# Revit family: Ray L-78
name_source: partatom
category: Lighting Fixtures
revit_build: Autodesk Revit 2014 (Build: 20140709_2115(x64)
units: mm (PartAtom-declared; Revit-internal decimal feet)

## types (1)
- 78-1/4"L 20-1/4"W x 6"H
    Adjustable Suspension Height = 48"
    Cables = (2)3/64" stainless steel cables
    Canopy Type = Canopy
    Color Filter = 16777215
    Diffuser = White Opal Acrylic
    Dimming Compatibility = 0-10v
    Dimming Lamp Color Temperature Shift = <None>
    Driver = (2) 100W
    Emit from Line Length = 60"
    Hardware = Stainless Steel Cables
    Height = 6"
    Input = 120v-277v
    Intensity = LED System
    Length = 78 1/4"
    Light Source Symbol Size = 8"
    Manufacturer = LightArt
    Material Options = http://www.3-form.com
    Model = Ray L-78
    Shade = 3form Varia Ecoresin
    Standards = 6-8 week lead time
    Type Comments = Does not include lamp
Does not include lamp
    URL = http://lightart.com
    Wattage Comments = 14
    Width = 20 1/4"

## geometry (parser evidence)
native form markers: Sweep x11
no freeform markers — native parametric forms only
